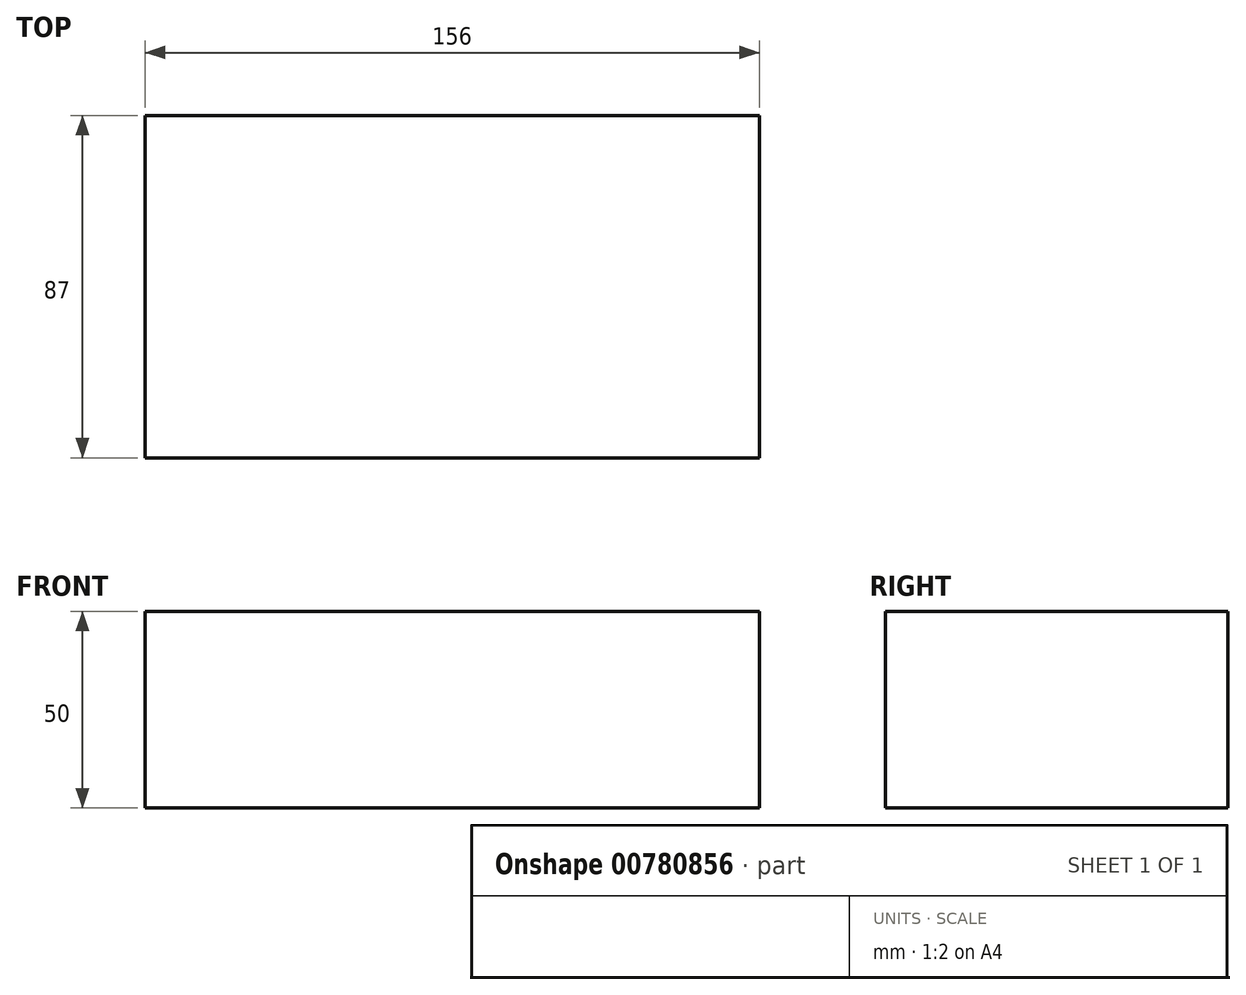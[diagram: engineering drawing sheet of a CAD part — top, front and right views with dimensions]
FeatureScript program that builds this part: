
annotation { "Feature Type Name" : "Feature", "Feature Type Description" : "" }
export const myFeature = defineFeature(function(context is Context, id is Id, definition is map)
    precondition{}
    {
        {
            var Q0;
            Q0=qCreatedBy(makeId("Front.planeOp"),FACE);
            var sketch = newSketch(context, id + "F0", { "sketchPlane" : qUnion([Q0])});
            skLineSegment(sketch, "E0", {"start": v(-68.03, 32.88) * mm, "end": v(-68.03, -17.12) * mm});
            skLineSegment(sketch, "E1", {"start": v(87.97, -17.12) * mm, "end": v(87.97, 32.88) * mm});
            skLineSegment(sketch, "E2", {"start": v(87.97, 32.88) * mm, "end": v(-68.03, 32.88) * mm});
            skLineSegment(sketch, "E3", {"start": v(-68.03, -17.12) * mm, "end": v(87.97, -17.12) * mm});
            skSolve(sketch);
        }
        {
            var Q0;
            Q0 = qSketchRegion(id + "F0", true);
            extrude(context, id + "F1", {"entities" : qUnion([Q0]), "depth" : 87 * mm, "offsetDistance" : 25 * mm});
        }
    });
